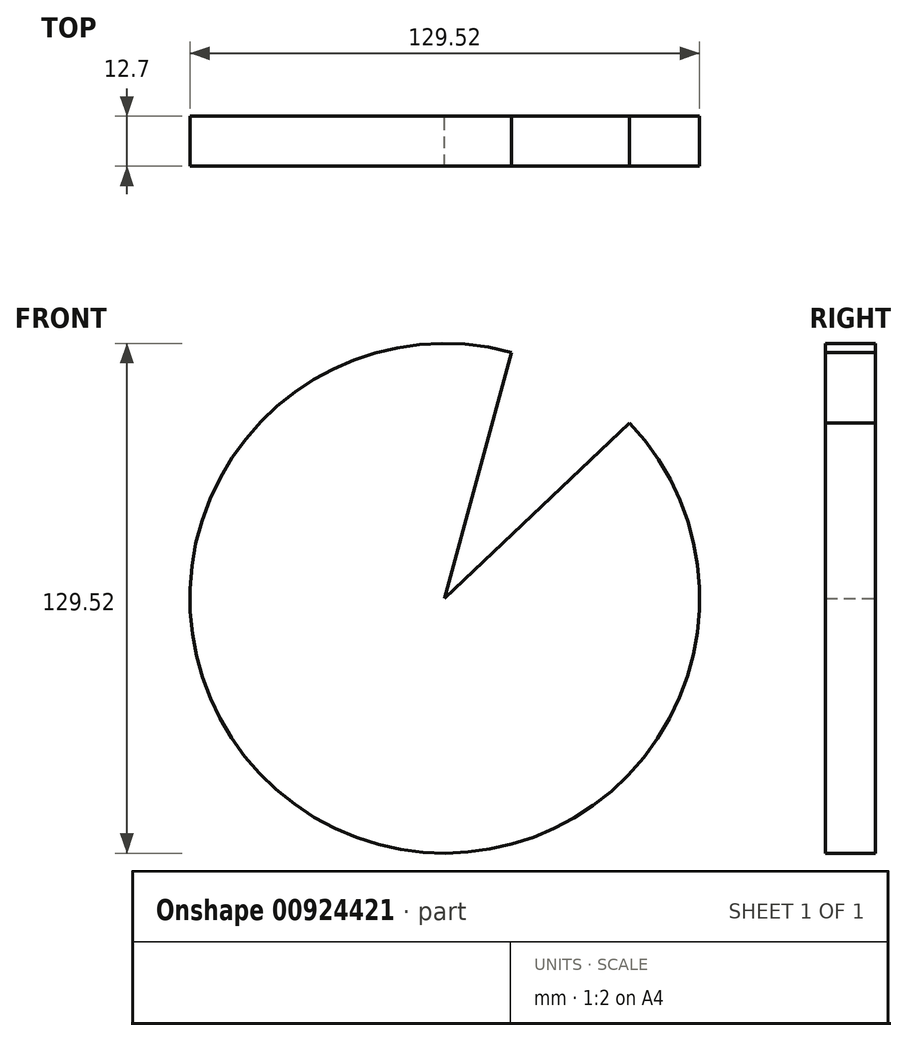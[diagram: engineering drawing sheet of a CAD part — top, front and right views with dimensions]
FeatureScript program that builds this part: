
annotation { "Feature Type Name" : "Feature", "Feature Type Description" : "" }
export const myFeature = defineFeature(function(context is Context, id is Id, definition is map)
    precondition{}
    {
        {
            var Q0;
            Q0=qCreatedBy(makeId("Front.planeOp"),FACE);
            var sketch = newSketch(context, id + "F0", { "sketchPlane" : qUnion([Q0])});
            skCircle(sketch, "E0", {"center": v(0, 0) * mm, "radius": 64.76 * mm});
            skLineSegment(sketch, "E1", {"start": v(0, 0) * mm, "end": v(16.93, 62.5) * mm});
            skLineSegment(sketch, "E2", {"start": v(0, 0) * mm, "end": v(46.97, 44.58) * mm});
            skSolve(sketch);
        }
        {
            var Q0;
            {var subQ0=sQuery(id+"F0.wireOp",EDGE,"E1");Q0=makeQuery(id+"F0.imprint","IMPRINT",FACE,{"disambiguationData":[TD([[makeQuery(id+"F0.imprint","IMPRINT",EDGE,{"derivedFrom":subQ0}),1.0]])]});}
            extrude(context, id + "F1", {"entities" : qUnion([Q0]), "depth" : 12.7 * mm, "offsetDistance" : 25.4 * mm});
        }
    });
